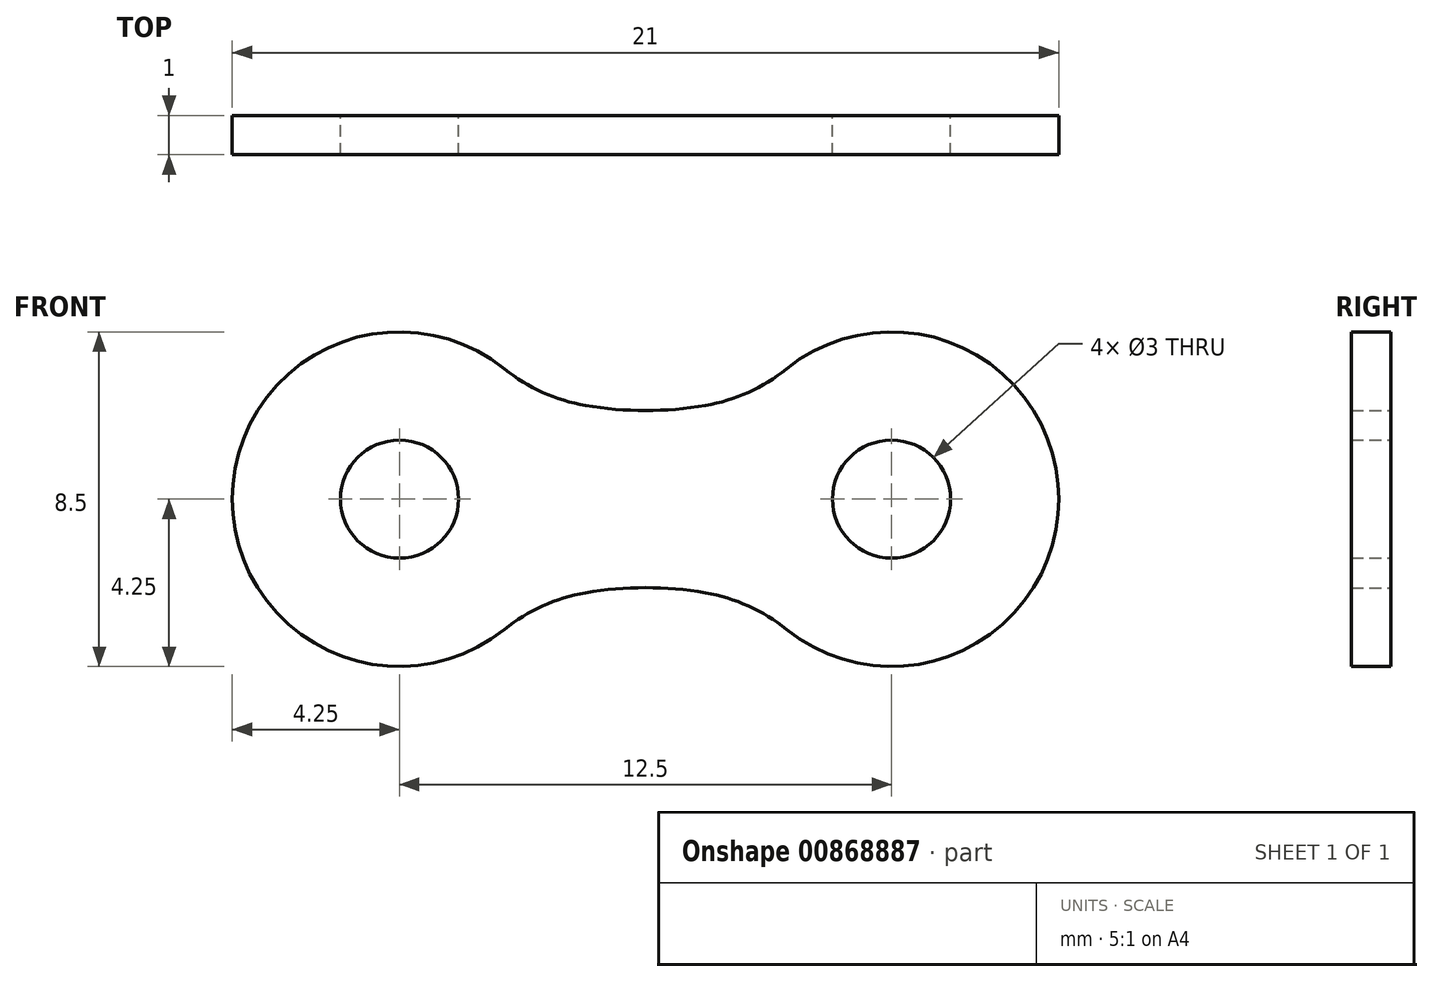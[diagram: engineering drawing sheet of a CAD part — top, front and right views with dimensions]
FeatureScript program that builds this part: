
annotation { "Feature Type Name" : "Feature", "Feature Type Description" : "" }
export const myFeature = defineFeature(function(context is Context, id is Id, definition is map)
    precondition{}
    {
        {
            var Q0;
            Q0=qCreatedBy(makeId("Front.planeOp"),FACE);
            var sketch = newSketch(context, id + "F0", { "sketchPlane" : qUnion([Q0])});
            skArc(sketch, "E0", {"start": v(2.67, 3.31) * mm, "mid": v(-4.25, 0) * mm, "end": v(2.67, -3.31) * mm});
            skArc(sketch, "E1", {"start": v(9.83, -3.31) * mm, "mid": v(16.75, 0) * mm, "end": v(9.83, 3.31) * mm});
            skLineSegment(sketch, "E2", {"start": v(0, 0) * mm, "end": v(12.5, 0) * mm, "construction": true});
            skLineSegment(sketch, "E3", {"start": v(6.25, -2.25) * mm, "end": v(6.25, 0) * mm, "construction": true});
            skPoint(sketch, "E4.start.orphan", {"position": v(0, 4.25) * mm});
            skPoint(sketch, "E5.start.orphan", {"position": v(0, -4.25) * mm});
            skArc(sketch, "E6", {"start": v(7.77, -2.38) * mm, "mid": v(6.25, -2.25) * mm, "end": v(4.73, -2.38) * mm});
            skLineSegment(sketch, "E7", {"start": v(3.22, -2.78) * mm, "end": v(9.28, -2.78) * mm, "construction": true});
            skArc(sketch, "E8", {"start": v(4.73, 2.38) * mm, "mid": v(6.25, 2.25) * mm, "end": v(7.77, 2.38) * mm});
            skLineSegment(sketch, "E9", {"start": v(3.22, 2.78) * mm, "end": v(9.28, 2.78) * mm, "construction": true});
            skLineSegment(sketch, "E10", {"start": v(6.25, 2.25) * mm, "end": v(6.25, 0) * mm, "construction": true});
            skPoint(sketch, "E11.visualSharp", {"position": v(3.22, 2.78) * mm});
            skArc(sketch, "E11.filletArc", {"start": v(2.67, 3.31) * mm, "mid": v(3.64, 2.71) * mm, "end": v(4.73, 2.38) * mm});
            skPoint(sketch, "E12.visualSharp", {"position": v(9.28, 2.78) * mm});
            skArc(sketch, "E12.filletArc", {"start": v(7.77, 2.38) * mm, "mid": v(8.86, 2.71) * mm, "end": v(9.83, 3.31) * mm});
            skPoint(sketch, "E13.visualSharp", {"position": v(9.28, -2.78) * mm});
            skArc(sketch, "E13.filletArc", {"start": v(9.83, -3.31) * mm, "mid": v(8.86, -2.71) * mm, "end": v(7.77, -2.38) * mm});
            skPoint(sketch, "E14.visualSharp", {"position": v(3.22, -2.78) * mm});
            skArc(sketch, "E14.filletArc", {"start": v(4.73, -2.38) * mm, "mid": v(3.64, -2.71) * mm, "end": v(2.67, -3.31) * mm});
            skCircle(sketch, "E15", {"center": v(0, 0) * mm, "radius": 1.5 * mm});
            skCircle(sketch, "E16", {"center": v(12.5, 0) * mm, "radius": 1.5 * mm});
            skSolve(sketch);
        }
        {
            var Q0;
            Q0=makeQuery(id+"F0.imprint","IMPRINT",FACE,{"disambiguationData":[TD([[makeQuery(id+"F0.imprint","IMPRINT",EDGE,{"derivedFrom":sQuery(id+"F0.wireOp",EDGE,"E0")}),1.0]])]});
            extrude(context, id + "F1", {"entities" : qUnion([Q0]), "depth" : 1 * mm});
        }
        {
            var Q0;
            Q0=makeQuery(id+"F1.opExtrude","SWEPT_BODY",BODY,{"disambiguationData":[OSD([sQuery(id+"F0.wireOp",EDGE,"E0"),sQuery(id+"F0.wireOp",EDGE,"E1"),sQuery(id+"F0.wireOp",EDGE,"E6"),sQuery(id+"F0.wireOp",EDGE,"E8"),sQuery(id+"F0.wireOp",EDGE,"E11.filletArc"),sQuery(id+"F0.wireOp",EDGE,"E12.filletArc"),sQuery(id+"F0.wireOp",EDGE,"E13.filletArc"),sQuery(id+"F0.wireOp",EDGE,"E14.filletArc"),sQuery(id+"F0.wireOp",EDGE,"E15"),sQuery(id+"F0.wireOp",EDGE,"E16")])]});
            transform(context, id + "F2", {"entities" : qUnion([Q0]), "transformType" : TransformType.TRANSLATION_3D, "dx" : 0 * mm, "dy" : 0 * mm, "dz" : 0 * mm, "makeCopy" : true});
        }
    });
